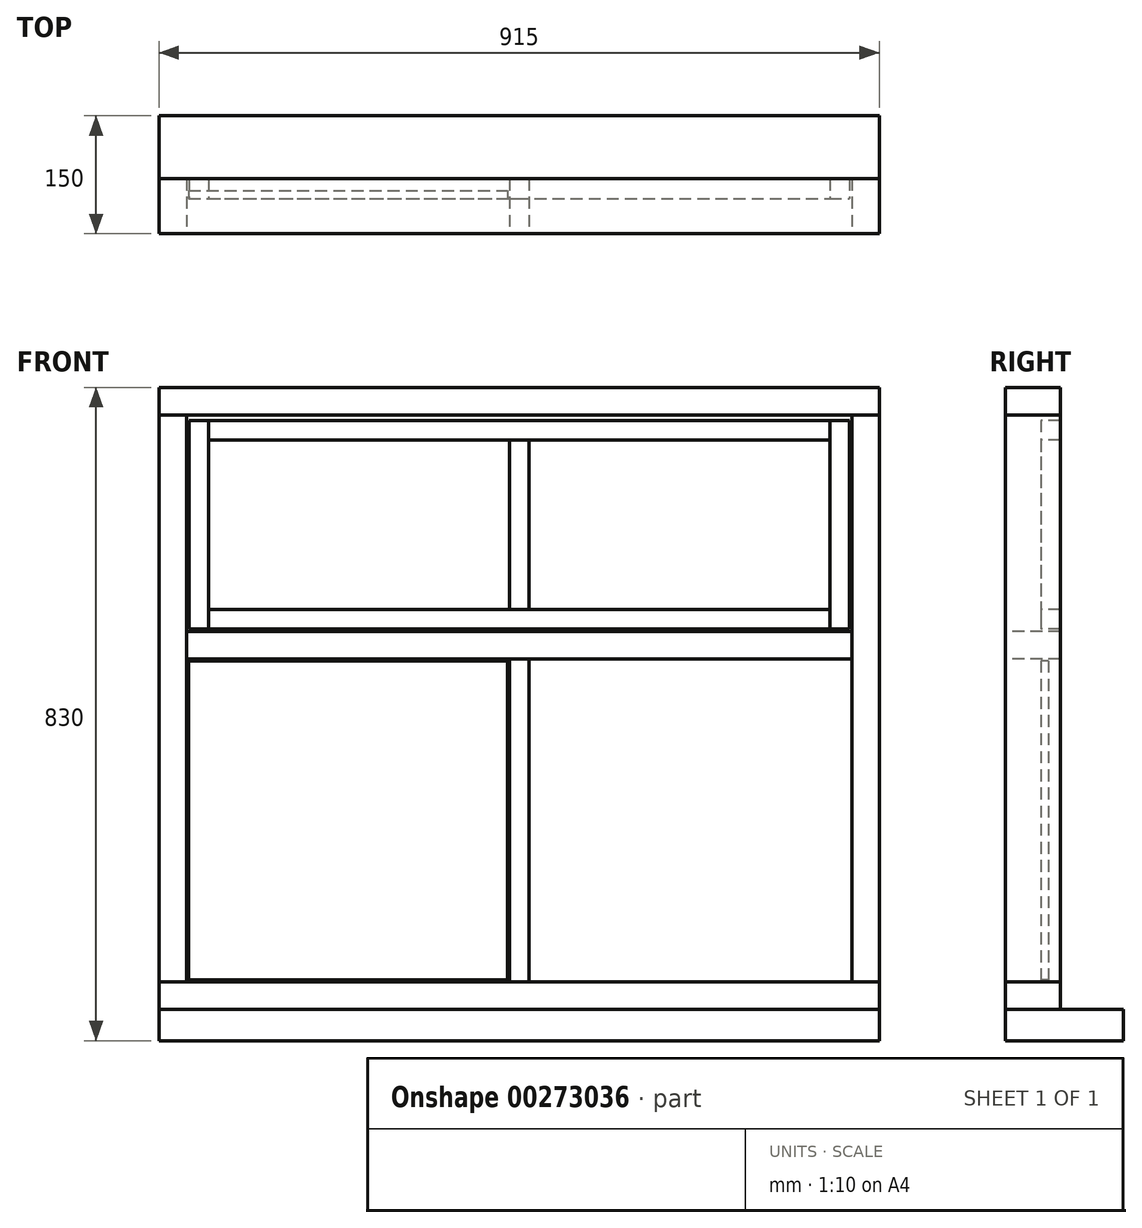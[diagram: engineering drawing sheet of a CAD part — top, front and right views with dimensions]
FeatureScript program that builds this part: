
annotation { "Feature Type Name" : "Feature", "Feature Type Description" : "" }
export const myFeature = defineFeature(function(context is Context, id is Id, definition is map)
    precondition{}
    {
        {
            var Q0;
            Q0=qCreatedBy(makeId("Front.planeOp"),FACE);
            var sketch = newSketch(context, id + "F0", { "sketchPlane" : qUnion([Q0])});
            skLineSegment(sketch, "E0.bottom", {"start": v(0, 0) * mm, "end": v(915, 0) * mm});
            skLineSegment(sketch, "E0.top", {"start": v(0, -830) * mm, "end": v(915, -830) * mm});
            skLineSegment(sketch, "E0.left", {"start": v(0, 0) * mm, "end": v(0, -790) * mm});
            skLineSegment(sketch, "E0.right", {"start": v(915, 0) * mm, "end": v(915, -790) * mm});
            skLineSegment(sketch, "E1", {"start": v(457.5, 0) * mm, "end": v(457.5, -830) * mm, "construction": true});
            skLineSegment(sketch, "E2", {"start": v(0, -310) * mm, "end": v(915, -310) * mm});
            skLineSegment(sketch, "E3", {"start": v(0, -35) * mm, "end": v(915, -35) * mm});
            skLineSegment(sketch, "E4", {"start": v(880, 0) * mm, "end": v(880, -790) * mm});
            skLineSegment(sketch, "E5", {"start": v(35, -790) * mm, "end": v(35, 0) * mm});
            skLineSegment(sketch, "E6", {"start": v(0, -830) * mm, "end": v(0, -790) * mm});
            skLineSegment(sketch, "E7", {"start": v(0, -790) * mm, "end": v(915, -790) * mm});
            skLineSegment(sketch, "E8", {"start": v(915, -790) * mm, "end": v(915, -830) * mm});
            skLineSegment(sketch, "E9", {"start": v(0, -345) * mm, "end": v(915, -345) * mm});
            skLineSegment(sketch, "E10", {"start": v(445, -310) * mm, "end": v(445, -830) * mm});
            skLineSegment(sketch, "E11", {"start": v(470, -310) * mm, "end": v(470, -830) * mm});
            skLineSegment(sketch, "E12", {"start": v(0, -755) * mm, "end": v(915, -755) * mm});
            skSolve(sketch);
        }
        {
            var Q0;
            Q0=qCreatedBy(makeId("Front.planeOp"),FACE);
            var sketch = newSketch(context, id + "F1", { "sketchPlane" : qUnion([Q0])});
            skLineSegment(sketch, "E13.bottom", {"start": v(38, -42) * mm, "end": v(877, -42) * mm});
            skLineSegment(sketch, "E13.top", {"start": v(38, -307) * mm, "end": v(877, -307) * mm});
            skLineSegment(sketch, "E13.left", {"start": v(38, -42) * mm, "end": v(38, -307) * mm});
            skLineSegment(sketch, "E13.right", {"start": v(877, -42) * mm, "end": v(877, -307) * mm});
            skLineSegment(sketch, "E14", {"start": v(63, -42) * mm, "end": v(63, -307) * mm});
            skLineSegment(sketch, "E15", {"start": v(852, -42) * mm, "end": v(852, -307) * mm});
            skLineSegment(sketch, "E16", {"start": v(38, -67) * mm, "end": v(877, -67) * mm});
            skLineSegment(sketch, "E17", {"start": v(38, -282) * mm, "end": v(877, -282) * mm});
            skLineSegment(sketch, "E18", {"start": v(445, -42) * mm, "end": v(445, -307) * mm});
            skLineSegment(sketch, "E19", {"start": v(470, -42) * mm, "end": v(470, -307) * mm});
            skSolve(sketch);
        }
        {
            var Q0;
            Q0=qCreatedBy(makeId("Front.planeOp"),FACE);
            var sketch = newSketch(context, id + "F2", { "sketchPlane" : qUnion([Q0])});
            skLineSegment(sketch, "E20.bottom", {"start": v(37.5, -752.5) * mm, "end": v(442.5, -752.5) * mm});
            skLineSegment(sketch, "E20.top", {"start": v(37.5, -347.5) * mm, "end": v(442.5, -347.5) * mm});
            skLineSegment(sketch, "E20.left", {"start": v(37.5, -347.5) * mm, "end": v(37.5, -752.5) * mm});
            skLineSegment(sketch, "E20.right", {"start": v(442.5, -347.5) * mm, "end": v(442.5, -752.5) * mm});
            skLineSegment(sketch, "E21.bottom", {"start": v(472.5, -752.5) * mm, "end": v(877.5, -752.5) * mm});
            skLineSegment(sketch, "E21.top", {"start": v(472.5, -347.5) * mm, "end": v(877.5, -347.5) * mm});
            skLineSegment(sketch, "E21.left", {"start": v(877.5, -347.5) * mm, "end": v(877.5, -752.5) * mm});
            skLineSegment(sketch, "E21.right", {"start": v(472.5, -347.5) * mm, "end": v(472.5, -752.5) * mm});
            skLineSegment(sketch, "E22", {"start": v(37.5, -550) * mm, "end": v(442.5, -550) * mm, "construction": true});
            skLineSegment(sketch, "E23", {"start": v(240, -347.5) * mm, "end": v(240, -752.5) * mm, "construction": true});
            skLineSegment(sketch, "E24", {"start": v(675, -347.5) * mm, "end": v(675, -752.5) * mm, "construction": true});
            skLineSegment(sketch, "E25.bottom", {"start": v(65.5, -279.5) * mm, "end": v(442.5, -279.5) * mm});
            skLineSegment(sketch, "E25.top", {"start": v(65.5, -69.5) * mm, "end": v(442.5, -69.5) * mm});
            skLineSegment(sketch, "E25.left", {"start": v(442.5, -69.5) * mm, "end": v(442.5, -279.5) * mm});
            skLineSegment(sketch, "E25.right", {"start": v(65.5, -69.5) * mm, "end": v(65.5, -279.5) * mm});
            skLineSegment(sketch, "E26.bottom", {"start": v(472.5, -279.5) * mm, "end": v(849.5, -279.5) * mm});
            skLineSegment(sketch, "E26.top", {"start": v(472.5, -69.5) * mm, "end": v(849.5, -69.5) * mm});
            skLineSegment(sketch, "E26.left", {"start": v(472.5, -69.5) * mm, "end": v(472.5, -279.5) * mm});
            skLineSegment(sketch, "E26.right", {"start": v(849.5, -69.5) * mm, "end": v(849.5, -279.5) * mm});
            skLineSegment(sketch, "E27", {"start": v(254, -69.5) * mm, "end": v(254, -279.5) * mm, "construction": true});
            skLineSegment(sketch, "E28", {"start": v(65.5, -174.5) * mm, "end": v(442.5, -174.5) * mm, "construction": true});
            skLineSegment(sketch, "E29", {"start": v(661, -69.5) * mm, "end": v(661, -279.5) * mm, "construction": true});
            skSolve(sketch);
        }
        {
            var Q0;
            Q0=qCreatedBy(makeId("Top.planeOp"),FACE);
            var sketch = newSketch(context, id + "F3", { "sketchPlane" : qUnion([Q0])});
            skLineSegment(sketch, "E30.bottom", {"start": v(0, 0) * mm, "end": v(915, 0) * mm});
            skLineSegment(sketch, "E30.top", {"start": v(0, 70) * mm, "end": v(915, 70) * mm});
            skLineSegment(sketch, "E30.left", {"start": v(0, 0) * mm, "end": v(0, 70) * mm});
            skLineSegment(sketch, "E30.right", {"start": v(915, 0) * mm, "end": v(915, 70) * mm});
            skLineSegment(sketch, "E31", {"start": v(35, 0) * mm, "end": v(35, 70) * mm});
            skLineSegment(sketch, "E32", {"start": v(35, 5) * mm, "end": v(35, 5) * mm});
            skLineSegment(sketch, "E33", {"start": v(45, 15) * mm, "end": v(45, 43) * mm});
            skLineSegment(sketch, "E34", {"start": v(45, 43) * mm, "end": v(35, 43) * mm});
            skPoint(sketch, "E35.visualSharp", {"position": v(45, 5) * mm});
            skArc(sketch, "E35.filletArc", {"start": v(35, 5) * mm, "mid": v(42.07, 7.93) * mm, "end": v(45, 15) * mm});
            skLineSegment(sketch, "E36.bottom", {"start": v(37.5, 55) * mm, "end": v(442.5, 55) * mm});
            skLineSegment(sketch, "E36.top", {"start": v(37.5, 45) * mm, "end": v(442.5, 45) * mm});
            skLineSegment(sketch, "E36.left", {"start": v(37.5, 55) * mm, "end": v(37.5, 45) * mm});
            skLineSegment(sketch, "E36.right", {"start": v(442.5, 55) * mm, "end": v(442.5, 45) * mm});
            skLineSegment(sketch, "E37", {"start": v(37.5, 45) * mm, "end": v(37.5, 0) * mm, "construction": true});
            skLineSegment(sketch, "E38", {"start": v(442.5, 45) * mm, "end": v(442.5, 0) * mm, "construction": true});
            skLineSegment(sketch, "E39", {"start": v(37.5, 48) * mm, "end": v(442.5, 48) * mm});
            skLineSegment(sketch, "E40", {"start": v(442.5, 52) * mm, "end": v(37.5, 52) * mm});
            skPoint(sketch, "E40.endSnap0", {"position": v(37.5, 50) * mm});
            skLineSegment(sketch, "E41", {"start": v(42.5, 52) * mm, "end": v(42.5, 48) * mm});
            skLineSegment(sketch, "E42", {"start": v(457.5, 70) * mm, "end": v(457.5, 0) * mm, "construction": true});
            skArc(sketch, "E43.MirrorCS", {"start": v(880, 5) * mm, "mid": v(872.93, 7.93) * mm, "end": v(870, 15) * mm});
            skLineSegment(sketch, "E44.MirrorCS", {"start": v(870, 15) * mm, "end": v(870, 43) * mm});
            skLineSegment(sketch, "E45.MirrorCS", {"start": v(870, 43) * mm, "end": v(880, 43) * mm});
            skLineSegment(sketch, "E46.MirrorCS", {"start": v(880, 0) * mm, "end": v(880, 70) * mm});
            skLineSegment(sketch, "E47.bottom", {"start": v(877, 70) * mm, "end": v(470, 70) * mm});
            skLineSegment(sketch, "E47.top", {"start": v(877, 45) * mm, "end": v(470, 45) * mm});
            skLineSegment(sketch, "E47.left", {"start": v(877, 70) * mm, "end": v(877, 45) * mm});
            skLineSegment(sketch, "E47.right", {"start": v(470, 70) * mm, "end": v(470, 45) * mm});
            skLineSegment(sketch, "E48", {"start": v(877, 45) * mm, "end": v(877, 0) * mm, "construction": true});
            skLineSegment(sketch, "E49.bottom", {"start": v(849.5, 75) * mm, "end": v(472.5, 75) * mm});
            skLineSegment(sketch, "E49.top", {"start": v(849.5, 65) * mm, "end": v(472.5, 65) * mm});
            skLineSegment(sketch, "E49.left", {"start": v(849.5, 75) * mm, "end": v(849.5, 65) * mm});
            skLineSegment(sketch, "E49.right", {"start": v(472.5, 75) * mm, "end": v(472.5, 65) * mm});
            skLineSegment(sketch, "E50", {"start": v(849.5, 65) * mm, "end": v(849.5, 0) * mm, "construction": true});
            skLineSegment(sketch, "E51", {"start": v(849.5, 68) * mm, "end": v(472.5, 68) * mm});
            skLineSegment(sketch, "E52", {"start": v(849.5, 72) * mm, "end": v(472.5, 72) * mm});
            skLineSegment(sketch, "E53", {"start": v(844.5, 72) * mm, "end": v(844.5, 68) * mm});
            skLineSegment(sketch, "E54", {"start": v(472.5, 65) * mm, "end": v(472.5, 0) * mm, "construction": true});
            skLineSegment(sketch, "E55", {"start": v(470, 45) * mm, "end": v(470, 0) * mm, "construction": true});
            skLineSegment(sketch, "E56", {"start": v(852, 70) * mm, "end": v(852, 45) * mm});
            skLineSegment(sketch, "E57", {"start": v(852, 45) * mm, "end": v(852, 0) * mm, "construction": true});
            skLineSegment(sketch, "E58.bottom", {"start": v(852, 70) * mm, "end": v(887, 70) * mm});
            skLineSegment(sketch, "E58.top", {"start": v(852, 85) * mm, "end": v(877, 85) * mm});
            skLineSegment(sketch, "E58.left", {"start": v(852, 70) * mm, "end": v(852, 85) * mm});
            skLineSegment(sketch, "E58.right", {"start": v(887, 70) * mm, "end": v(887, 75) * mm});
            skLineSegment(sketch, "E59", {"start": v(852, 63) * mm, "end": v(842, 63) * mm});
            skLineSegment(sketch, "E60", {"start": v(842, 63) * mm, "end": v(842, 60) * mm});
            skLineSegment(sketch, "E61", {"start": v(852, 50) * mm, "end": v(852, 50) * mm});
            skPoint(sketch, "E62.visualSharp", {"position": v(842, 50) * mm});
            skArc(sketch, "E62.filletArc", {"start": v(842, 60) * mm, "mid": v(844.93, 52.93) * mm, "end": v(852, 50) * mm});
            skPoint(sketch, "E63.visualSharp", {"position": v(887, 85) * mm});
            skArc(sketch, "E63.filletArc", {"start": v(887, 75) * mm, "mid": v(884.07, 82.07) * mm, "end": v(877, 85) * mm});
            skSolve(sketch);
        }
        {
            var Q0;
            Q0=qCreatedBy(makeId("Front.planeOp"),FACE);
            var sketch = newSketch(context, id + "F4", { "sketchPlane" : qUnion([Q0])});
            skLineSegment(sketch, "E64.bottom", {"start": v(0, 0) * mm, "end": v(915, 0) * mm});
            skLineSegment(sketch, "E64.top", {"start": v(0, -35) * mm, "end": v(915, -35) * mm});
            skLineSegment(sketch, "E64.left", {"start": v(0, 0) * mm, "end": v(0, -35) * mm});
            skLineSegment(sketch, "E64.right", {"start": v(915, 0) * mm, "end": v(915, -35) * mm});
            skSolve(sketch);
        }
        {
            var Q0;
            Q0=qCreatedBy(makeId("Front.planeOp"),FACE);
            var sketch = newSketch(context, id + "F5", { "sketchPlane" : qUnion([Q0])});
            skLineSegment(sketch, "E65.bottom", {"start": v(0, -755) * mm, "end": v(915, -755) * mm});
            skLineSegment(sketch, "E65.top", {"start": v(0, -790) * mm, "end": v(915, -790) * mm});
            skLineSegment(sketch, "E65.left", {"start": v(0, -755) * mm, "end": v(0, -790) * mm});
            skLineSegment(sketch, "E65.right", {"start": v(915, -755) * mm, "end": v(915, -790) * mm});
            skSolve(sketch);
        }
        {
            var Q0;
            Q0=qCreatedBy(makeId("Front.planeOp"),FACE);
            var sketch = newSketch(context, id + "F6", { "sketchPlane" : qUnion([Q0])});
            skLineSegment(sketch, "E66.bottom", {"start": v(35, -310) * mm, "end": v(880, -310) * mm});
            skLineSegment(sketch, "E66.top", {"start": v(35, -345) * mm, "end": v(880, -345) * mm});
            skLineSegment(sketch, "E66.left", {"start": v(35, -310) * mm, "end": v(35, -345) * mm});
            skLineSegment(sketch, "E66.right", {"start": v(880, -310) * mm, "end": v(880, -345) * mm});
            skSolve(sketch);
        }
        {
            var Q0;
            Q0=qCreatedBy(makeId("Front.planeOp"),FACE);
            var sketch = newSketch(context, id + "F7", { "sketchPlane" : qUnion([Q0])});
            skLineSegment(sketch, "E67.bottom", {"start": v(0, -35) * mm, "end": v(35, -35) * mm});
            skLineSegment(sketch, "E67.top", {"start": v(0, -755) * mm, "end": v(35, -755) * mm});
            skLineSegment(sketch, "E67.left", {"start": v(0, -35) * mm, "end": v(0, -755) * mm});
            skLineSegment(sketch, "E67.right", {"start": v(35, -35) * mm, "end": v(35, -755) * mm});
            skSolve(sketch);
        }
        {
            var Q0;
            Q0=qCreatedBy(makeId("Front.planeOp"),FACE);
            var sketch = newSketch(context, id + "F8", { "sketchPlane" : qUnion([Q0])});
            skLineSegment(sketch, "E68.bottom", {"start": v(880, -35) * mm, "end": v(915, -35) * mm});
            skLineSegment(sketch, "E68.top", {"start": v(880, -755) * mm, "end": v(915, -755) * mm});
            skLineSegment(sketch, "E68.left", {"start": v(880, -35) * mm, "end": v(880, -755) * mm});
            skLineSegment(sketch, "E68.right", {"start": v(915, -35) * mm, "end": v(915, -755) * mm});
            skSolve(sketch);
        }
        {
            var Q0;
            Q0=qCreatedBy(makeId("Front.planeOp"),FACE);
            var sketch = newSketch(context, id + "F9", { "sketchPlane" : qUnion([Q0])});
            skLineSegment(sketch, "E69.bottom", {"start": v(445, -345) * mm, "end": v(470, -345) * mm});
            skLineSegment(sketch, "E69.top", {"start": v(445, -755) * mm, "end": v(470, -755) * mm});
            skLineSegment(sketch, "E69.left", {"start": v(445, -345) * mm, "end": v(445, -755) * mm});
            skLineSegment(sketch, "E69.right", {"start": v(470, -345) * mm, "end": v(470, -755) * mm});
            skSolve(sketch);
        }
        {
            var Q0;
            Q0=qCreatedBy(makeId("Front.planeOp"),FACE);
            var sketch = newSketch(context, id + "F10", { "sketchPlane" : qUnion([Q0])});
            skLineSegment(sketch, "E70.bottom", {"start": v(0, -790) * mm, "end": v(915, -790) * mm});
            skLineSegment(sketch, "E70.top", {"start": v(0, -830) * mm, "end": v(915, -830) * mm});
            skLineSegment(sketch, "E70.left", {"start": v(0, -790) * mm, "end": v(0, -830) * mm});
            skLineSegment(sketch, "E70.right", {"start": v(915, -790) * mm, "end": v(915, -830) * mm});
            skSolve(sketch);
        }
        {
            var Q0;
            Q0 = qSketchRegion(id + "F4", true);
            var Q1;
            Q1=sQuery(id+"F3.wireOp",VERTEX,"E30.left.end");
            extrude(context, id + "F11", {"entities" : qUnion([Q0]), "endBound" : BoundingType.UP_TO_VERTEX, "oppositeDirection" : true, "endBoundEntityVertex" : qUnion([Q1]), "depth" : 25 * mm});
        }
        {
            var Q0;
            Q0 = qSketchRegion(id + "F5", true);
            var Q1;
            Q1=sQuery(id+"F3.wireOp",VERTEX,"E30.left.end");
            extrude(context, id + "F12", {"entities" : qUnion([Q0]), "endBound" : BoundingType.UP_TO_VERTEX, "oppositeDirection" : true, "endBoundEntityVertex" : qUnion([Q1]), "depth" : 25 * mm});
        }
        {
            var Q0;
            Q0 = qSketchRegion(id + "F6", true);
            var Q1;
            Q1=sQuery(id+"F3.wireOp",VERTEX,"E30.left.end");
            extrude(context, id + "F13", {"entities" : qUnion([Q0]), "endBound" : BoundingType.UP_TO_VERTEX, "oppositeDirection" : true, "endBoundEntityVertex" : qUnion([Q1]), "depth" : 25 * mm});
        }
        {
            var Q0;
            Q0 = qSketchRegion(id + "F7", true);
            var Q1;
            Q1=sQuery(id+"F3.wireOp",VERTEX,"E30.left.end");
            extrude(context, id + "F14", {"entities" : qUnion([Q0]), "endBound" : BoundingType.UP_TO_VERTEX, "oppositeDirection" : true, "endBoundEntityVertex" : qUnion([Q1]), "depth" : 25 * mm});
        }
        {
            var Q0;
            Q0 = qSketchRegion(id + "F8", true);
            var Q1;
            Q1=sQuery(id+"F3.wireOp",VERTEX,"E30.left.end");
            extrude(context, id + "F15", {"entities" : qUnion([Q0]), "endBound" : BoundingType.UP_TO_VERTEX, "oppositeDirection" : true, "endBoundEntityVertex" : qUnion([Q1]), "depth" : 25 * mm});
        }
        {
            var Q0;
            Q0 = qSketchRegion(id + "F9", true);
            var Q1;
            Q1=sQuery(id+"F3.wireOp",VERTEX,"E30.left.end");
            extrude(context, id + "F16", {"entities" : qUnion([Q0]), "endBound" : BoundingType.UP_TO_VERTEX, "oppositeDirection" : true, "endBoundEntityVertex" : qUnion([Q1]), "depth" : 25 * mm});
        }
        {
            var Q0;
            Q0=qCreatedBy(makeId("Front.planeOp"),FACE);
            var Q1;
            Q1=sQuery(id+"F3.wireOp",VERTEX,"E47.left.end");
            cPlane(context, id + "F17", {"entities" : qUnion([Q0, Q1]), "cplaneType" : CPlaneType.PLANE_POINT, "offset" : 25 * mm, "width" : 150 * mm, "height" : 150 * mm});
        }
        {
            var Q0;
            Q0=qCreatedBy(id+"F17.planeOp",FACE);
            var sketch = newSketch(context, id + "F18", { "sketchPlane" : qUnion([Q0])});
            skLineSegment(sketch, "E71.bottom", {"start": v(852, -42) * mm, "end": v(63, -42) * mm});
            skLineSegment(sketch, "E71.top", {"start": v(852, -67) * mm, "end": v(63, -67) * mm});
            skLineSegment(sketch, "E71.left", {"start": v(852, -42) * mm, "end": v(852, -67) * mm});
            skLineSegment(sketch, "E71.right", {"start": v(63, -42) * mm, "end": v(63, -67) * mm});
            skSolve(sketch);
        }
        {
            var Q0;
            Q0=qCreatedBy(id+"F17.planeOp",FACE);
            var sketch = newSketch(context, id + "F19", { "sketchPlane" : qUnion([Q0])});
            skLineSegment(sketch, "E72.bottom", {"start": v(63, -282) * mm, "end": v(852, -282) * mm});
            skLineSegment(sketch, "E72.top", {"start": v(63, -307) * mm, "end": v(852, -307) * mm});
            skLineSegment(sketch, "E72.left", {"start": v(63, -282) * mm, "end": v(63, -307) * mm});
            skLineSegment(sketch, "E72.right", {"start": v(852, -282) * mm, "end": v(852, -307) * mm});
            skSolve(sketch);
        }
        {
            var Q0;
            Q0=qCreatedBy(id+"F17.planeOp",FACE);
            var sketch = newSketch(context, id + "F20", { "sketchPlane" : qUnion([Q0])});
            skLineSegment(sketch, "E73.bottom", {"start": v(38, -42) * mm, "end": v(63, -42) * mm});
            skLineSegment(sketch, "E73.top", {"start": v(38, -307) * mm, "end": v(63, -307) * mm});
            skLineSegment(sketch, "E73.left", {"start": v(38, -42) * mm, "end": v(38, -307) * mm});
            skLineSegment(sketch, "E73.right", {"start": v(63, -42) * mm, "end": v(63, -307) * mm});
            skSolve(sketch);
        }
        {
            var Q0;
            Q0=qCreatedBy(id+"F17.planeOp",FACE);
            var sketch = newSketch(context, id + "F21", { "sketchPlane" : qUnion([Q0])});
            skLineSegment(sketch, "E74.bottom", {"start": v(852, -42) * mm, "end": v(877, -42) * mm});
            skLineSegment(sketch, "E74.top", {"start": v(852, -307) * mm, "end": v(877, -307) * mm});
            skLineSegment(sketch, "E74.left", {"start": v(852, -42) * mm, "end": v(852, -307) * mm});
            skLineSegment(sketch, "E74.right", {"start": v(877, -42) * mm, "end": v(877, -307) * mm});
            skSolve(sketch);
        }
        {
            var Q0;
            Q0=qCreatedBy(id+"F17.planeOp",FACE);
            var sketch = newSketch(context, id + "F22", { "sketchPlane" : qUnion([Q0])});
            skLineSegment(sketch, "E75.bottom", {"start": v(445, -67) * mm, "end": v(470, -67) * mm});
            skLineSegment(sketch, "E75.top", {"start": v(445, -282) * mm, "end": v(470, -282) * mm});
            skLineSegment(sketch, "E75.left", {"start": v(445, -67) * mm, "end": v(445, -282) * mm});
            skLineSegment(sketch, "E75.right", {"start": v(470, -67) * mm, "end": v(470, -282) * mm});
            skSolve(sketch);
        }
        {
            var Q0;
            Q0 = qSketchRegion(id + "F18", true);
            var Q1;
            Q1=sQuery(id+"F3.wireOp",VERTEX,"E30.left.end");
            extrude(context, id + "F23", {"entities" : qUnion([Q0]), "endBound" : BoundingType.UP_TO_VERTEX, "oppositeDirection" : true, "endBoundEntityVertex" : qUnion([Q1]), "depth" : 25 * mm});
        }
        {
            var Q0;
            Q0 = qSketchRegion(id + "F19", true);
            var Q1;
            Q1=sQuery(id+"F3.wireOp",VERTEX,"E30.left.end");
            extrude(context, id + "F24", {"entities" : qUnion([Q0]), "endBound" : BoundingType.UP_TO_VERTEX, "oppositeDirection" : true, "endBoundEntityVertex" : qUnion([Q1]), "depth" : 25 * mm});
        }
        {
            var Q0;
            Q0 = qSketchRegion(id + "F20", true);
            var Q1;
            Q1=sQuery(id+"F3.wireOp",VERTEX,"E30.left.end");
            extrude(context, id + "F25", {"entities" : qUnion([Q0]), "endBound" : BoundingType.UP_TO_VERTEX, "oppositeDirection" : true, "endBoundEntityVertex" : qUnion([Q1]), "depth" : 25 * mm});
        }
        {
            var Q0;
            Q0 = qSketchRegion(id + "F21", true);
            var Q1;
            Q1=sQuery(id+"F3.wireOp",VERTEX,"E30.left.end");
            extrude(context, id + "F26", {"entities" : qUnion([Q0]), "endBound" : BoundingType.UP_TO_VERTEX, "oppositeDirection" : true, "endBoundEntityVertex" : qUnion([Q1]), "depth" : 25 * mm});
        }
        {
            var Q0;
            Q0 = qSketchRegion(id + "F22", true);
            var Q1;
            Q1=sQuery(id+"F3.wireOp",VERTEX,"E30.left.end");
            extrude(context, id + "F27", {"entities" : qUnion([Q0]), "endBound" : BoundingType.UP_TO_VERTEX, "oppositeDirection" : true, "endBoundEntityVertex" : qUnion([Q1]), "depth" : 25 * mm});
        }
        {
            var Q0;
            Q0=qCreatedBy(makeId("Front.planeOp"),FACE);
            var Q1;
            Q1=sQuery(id+"F3.wireOp",VERTEX,"E36.left.end");
            cPlane(context, id + "F28", {"entities" : qUnion([Q0, Q1]), "cplaneType" : CPlaneType.PLANE_POINT, "offset" : 25 * mm, "width" : 150 * mm, "height" : 150 * mm});
        }
        {
            var Q0;
            Q0=qCreatedBy(id+"F28.planeOp",FACE);
            var sketch = newSketch(context, id + "F29", { "sketchPlane" : qUnion([Q0])});
            skLineSegment(sketch, "E76.bottom", {"start": v(37.5, -347.5) * mm, "end": v(442.5, -347.5) * mm});
            skLineSegment(sketch, "E76.top", {"start": v(37.5, -752.5) * mm, "end": v(442.5, -752.5) * mm});
            skLineSegment(sketch, "E76.left", {"start": v(37.5, -347.5) * mm, "end": v(37.5, -752.5) * mm});
            skLineSegment(sketch, "E76.right", {"start": v(442.5, -347.5) * mm, "end": v(442.5, -752.5) * mm});
            skSolve(sketch);
        }
        {
            var Q0;
            Q0 = qSketchRegion(id + "F29", true);
            var Q1;
            Q1=sQuery(id+"F3.wireOp",VERTEX,"E36.left.start");
            extrude(context, id + "F30", {"entities" : qUnion([Q0]), "endBound" : BoundingType.UP_TO_VERTEX, "oppositeDirection" : true, "endBoundEntityVertex" : qUnion([Q1]), "depth" : 25 * mm});
        }
        {
            var Q0;
            Q0=makeQuery(id+"F10.imprint","IMPRINT",FACE,{"disambiguationData":[TD([[makeQuery(id+"F10.imprint","IMPRINT",EDGE,{"derivedFrom":sQuery(id+"F10.wireOp",EDGE,"E70.bottom")}),-1.0]])]});
            extrude(context, id + "F31", {"entities" : qUnion([Q0]), "oppositeDirection" : true, "depth" : (70 + 80) * mm});
        }
    });
